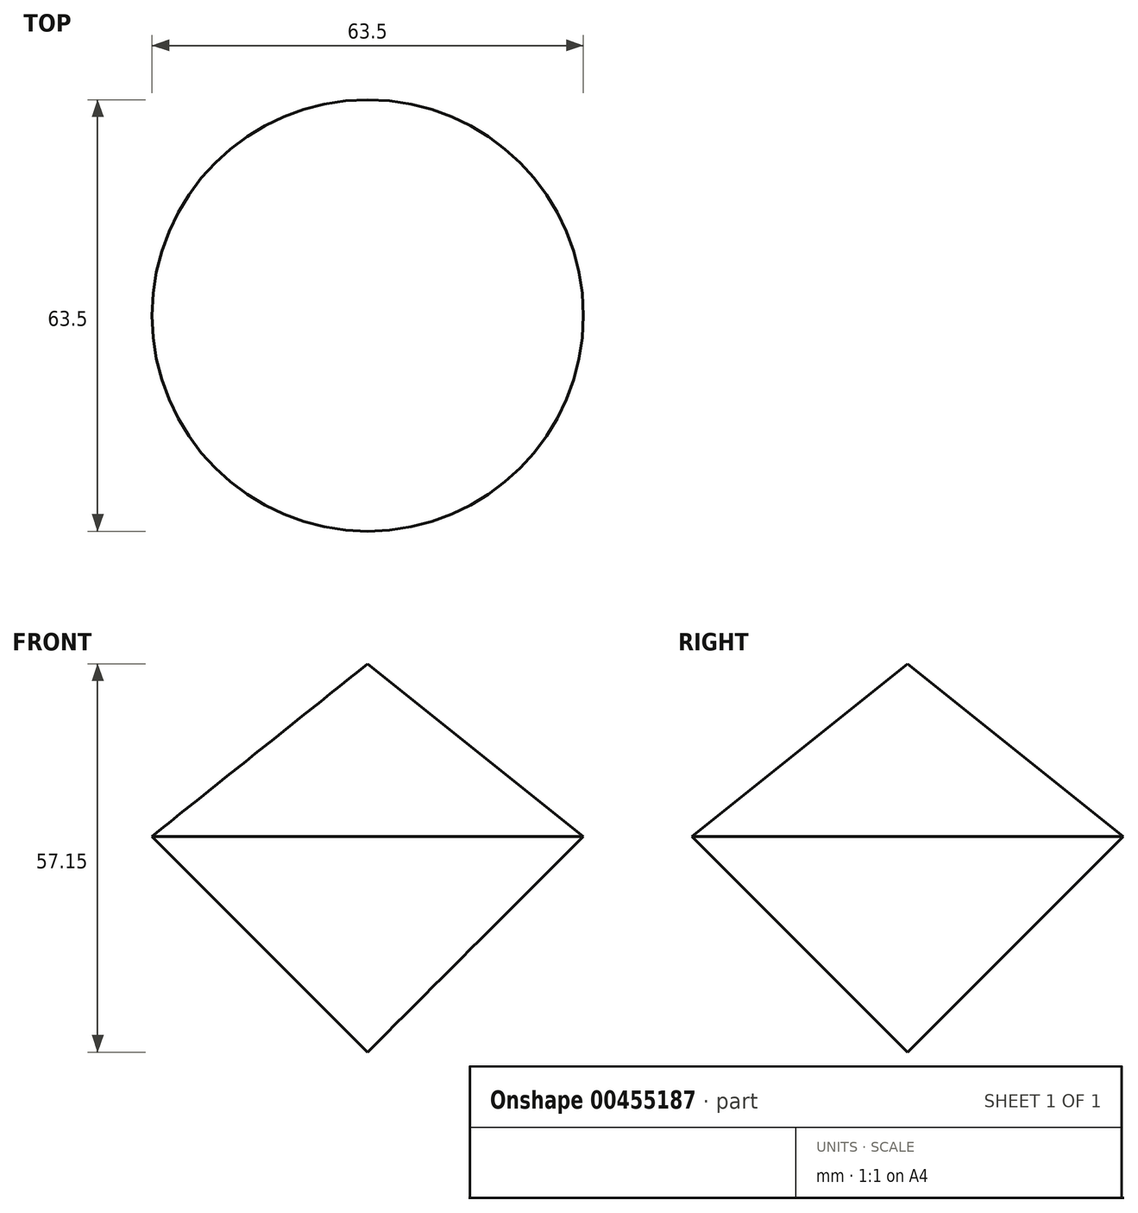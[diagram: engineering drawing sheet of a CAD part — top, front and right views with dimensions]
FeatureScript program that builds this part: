
annotation { "Feature Type Name" : "Feature", "Feature Type Description" : "" }
export const myFeature = defineFeature(function(context is Context, id is Id, definition is map)
    precondition{}
    {
        {
            var Q0;
            Q0=qCreatedBy(makeId("Top.planeOp"),FACE);
            var sketch = newSketch(context, id + "F0", { "sketchPlane" : qUnion([Q0])});
            skCircle(sketch, "E0", {"center": v(0, 0) * mm, "radius": 3.18 * mm});
            skSolve(sketch);
        }
        {
            var Q0;
            Q0=makeQuery(id+"F0.imprint","IMPRINT",FACE,{"disambiguationData":[TD([[makeQuery(id+"F0.imprint","IMPRINT",EDGE,{"derivedFrom":sQuery(id+"F0.wireOp",EDGE,"E0")}),1.0]])]});
            extrude(context, id + "F1", {"entities" : qUnion([Q0]), "oppositeDirection" : true, "depth" : 57.15 * mm});
        }
        {
            var Q0;
            Q0=qCreatedBy(makeId("Top.planeOp"),FACE);
            cPlane(context, id + "F2", {"entities" : qUnion([Q0]), "cplaneType" : CPlaneType.OFFSET, "offset" : 25.4 * mm, "oppositeDirection" : true, "width" : 152.4 * mm, "height" : 152.4 * mm});
        }
        {
            var Q0;
            Q0=qCreatedBy(id+"F2.planeOp",FACE);
            var sketch = newSketch(context, id + "F3", { "sketchPlane" : qUnion([Q0])});
            skCircle(sketch, "E1", {"center": v(0, 0) * mm, "radius": 38.1 * mm});
            skSolve(sketch);
        }
        {
            var Q0;
            Q0=makeQuery(id+"F3.imprint","IMPRINT",FACE,{"disambiguationData":[TD([[makeQuery(id+"F3.imprint","IMPRINT",EDGE,{"derivedFrom":sQuery(id+"F3.wireOp",EDGE,"E1")}),1.0]])]});
            extrude(context, id + "F4", {"entities" : qUnion([Q0]), "operationType" : NewBodyOperationType.ADD, "oppositeDirection" : true, "depth" : 31.75 * mm});
        }
        {
            var Q0;
            Q0=makeQuery(id+"F4.opExtrude","CAP_EDGE",EDGE,{"disambiguationData":[OSD([sQuery(id+"F3.wireOp",EDGE,"E1")])],"isStart":false});
            chamfer(context, id + "F5", {"entities" : qUnion([Q0]), "width" : 38.1 * mm, "tangentPropagation" : true});
        }
        {
            var Q0;
            Q0=makeQuery(id+"F4.opExtrude","CAP_FACE",FACE,{"disambiguationData":[OSD([sQuery(id+"F3.wireOp",EDGE,"E1")])],"isStart":true});
            extrude(context, id + "F6", {"entities" : qUnion([Q0]), "operationType" : NewBodyOperationType.ADD, "depth" : 25.4 * mm});
        }
        {
            var Q0;
            Q0=makeQuery(id+"F6.opExtrude","CAP_EDGE",EDGE,{"disambiguationData":[OSD([sQuery(id+"F3.wireOp",EDGE,"E1")])],"isStart":false});
            chamfer(context, id + "F7", {"entities" : qUnion([Q0]), "chamferType" : ChamferType.TWO_OFFSETS, "width1" : 31.75 * mm, "oppositeDirection" : false, "width2" : 25.4 * mm, "tangentPropagation" : true});
        }
    });
